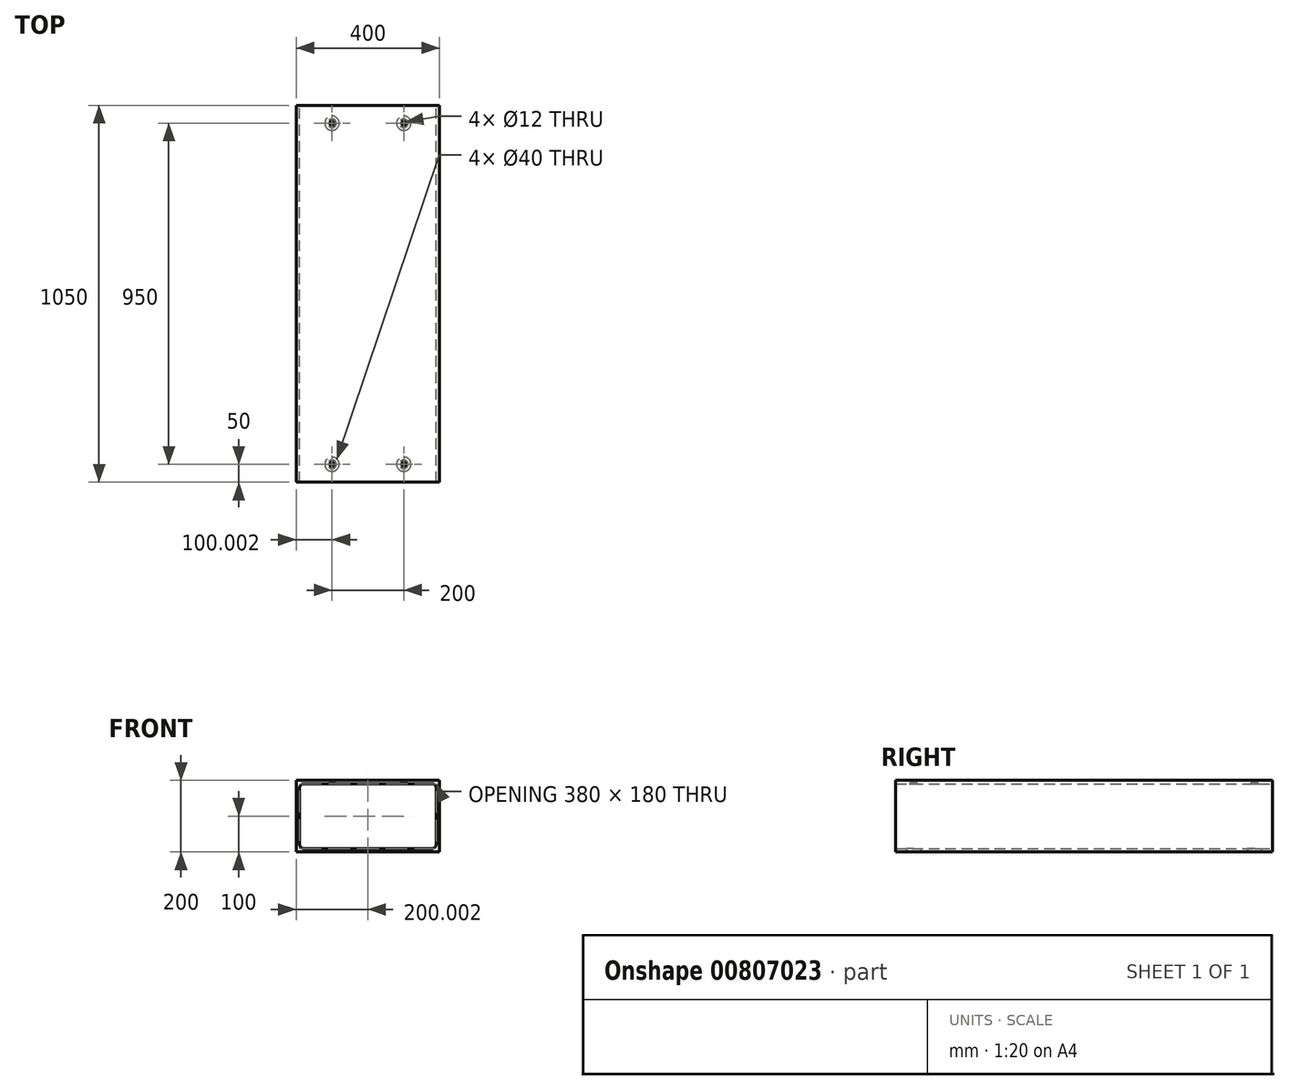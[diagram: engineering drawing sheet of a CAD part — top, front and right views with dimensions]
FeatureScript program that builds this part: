
annotation { "Feature Type Name" : "Feature", "Feature Type Description" : "" }
export const myFeature = defineFeature(function(context is Context, id is Id, definition is map)
    precondition{}
    {
        {
            var Q0;
            Q0=qCreatedBy(makeId("Front.planeOp"),FACE);
            var sketch = newSketch(context, id + "F0", { "sketchPlane" : qUnion([Q0])});
            skLineSegment(sketch, "E0.bottom", {"start": v(-139.55, 0) * mm, "end": v(260.45, 0) * mm});
            skLineSegment(sketch, "E0.top", {"start": v(-139.55, -200) * mm, "end": v(260.45, -200) * mm});
            skLineSegment(sketch, "E0.left", {"start": v(-139.55, 0) * mm, "end": v(-139.55, -200) * mm});
            skLineSegment(sketch, "E0.right", {"start": v(260.45, 0) * mm, "end": v(260.45, -200) * mm});
            skLineSegment(sketch, "E1.bottom", {"start": v(-119.55, -10) * mm, "end": v(240.45, -10) * mm});
            skLineSegment(sketch, "E1.top", {"start": v(-119.55, -190) * mm, "end": v(240.45, -190) * mm});
            skLineSegment(sketch, "E1.left", {"start": v(-129.55, -20) * mm, "end": v(-129.55, -180) * mm});
            skLineSegment(sketch, "E1.right", {"start": v(250.45, -20) * mm, "end": v(250.45, -180) * mm});
            skPoint(sketch, "E2.visualSharp", {"position": v(-129.55, -10) * mm});
            skArc(sketch, "E2.filletArc", {"start": v(-119.55, -10) * mm, "mid": v(-126.62, -12.93) * mm, "end": v(-129.55, -20) * mm});
            skPoint(sketch, "E3.visualSharp", {"position": v(250.45, -10) * mm});
            skArc(sketch, "E3.filletArc", {"start": v(250.45, -20) * mm, "mid": v(247.52, -12.93) * mm, "end": v(240.45, -10) * mm});
            skPoint(sketch, "E4.visualSharp", {"position": v(250.45, -190) * mm});
            skArc(sketch, "E4.filletArc", {"start": v(240.45, -190) * mm, "mid": v(247.52, -187.07) * mm, "end": v(250.45, -180) * mm});
            skPoint(sketch, "E5.visualSharp", {"position": v(-129.55, -190) * mm});
            skArc(sketch, "E5.filletArc", {"start": v(-129.55, -180) * mm, "mid": v(-126.62, -187.07) * mm, "end": v(-119.55, -190) * mm});
            skSolve(sketch);
        }
        {
            var Q0;
            Q0=makeQuery(id+"F0.imprint","IMPRINT",FACE,{"disambiguationData":[TD([[makeQuery(id+"F0.imprint","IMPRINT",EDGE,{"derivedFrom":sQuery(id+"F0.wireOp",EDGE,"E0.bottom")}),-1.0]])]});
            extrude(context, id + "F1", {"entities" : qUnion([Q0]), "endBound" : BoundingType.SYMMETRIC, "depth" : 1050 * mm, "offsetDistance" : 25 * mm});
        }
        {
            var Q0;
            Q0=makeQuery(id+"F1.opExtrude","SWEPT_FACE",FACE,{"disambiguationData":[OSD([sQuery(id+"F0.wireOp",EDGE,"E0.bottom")])]});
            var sketch = newSketch(context, id + "F2", { "sketchPlane" : qUnion([Q0])});
            skCircle(sketch, "E6", {"center": v(-39.55, -475) * mm, "radius": 6 * mm});
            skCircle(sketch, "E7", {"center": v(160.45, -475) * mm, "radius": 6 * mm});
            skCircle(sketch, "E8.MirrorC", {"center": v(-39.55, 475) * mm, "radius": 6 * mm});
            skCircle(sketch, "E9.MirrorC", {"center": v(160.45, 475) * mm, "radius": 6 * mm});
            skSolve(sketch);
        }
        {
            var Q0;
            Q0 = qSketchRegion(id + "F2", true);
            extrude(context, id + "F3", {"entities" : qUnion([Q0]), "operationType" : NewBodyOperationType.REMOVE, "endBound" : BoundingType.THROUGH_ALL, "oppositeDirection" : true, "depth" : 25 * mm, "offsetDistance" : 25 * mm});
        }
        {
            var Q0;
            Q0=makeQuery(id+"F1.opExtrude","SWEPT_FACE",FACE,{"disambiguationData":[OSD([sQuery(id+"F0.wireOp",EDGE,"E0.top")])]});
            var sketch = newSketch(context, id + "F4", { "sketchPlane" : qUnion([Q0])});
            skCircle(sketch, "E10", {"center": v(-39.55, 475) * mm, "radius": 20 * mm});
            skCircle(sketch, "E11", {"center": v(160.45, 475) * mm, "radius": 20 * mm});
            skCircle(sketch, "E12.MirrorC", {"center": v(-39.55, -475) * mm, "radius": 20 * mm});
            skCircle(sketch, "E13.MirrorC", {"center": v(160.45, -475) * mm, "radius": 20 * mm});
            skSolve(sketch);
        }
        {
            var Q0;
            Q0 = qSketchRegion(id + "F4", true);
            extrude(context, id + "F5", {"entities" : qUnion([Q0]), "operationType" : NewBodyOperationType.REMOVE, "oppositeDirection" : true, "depth" : 25 * mm, "offsetDistance" : 25 * mm});
        }
        {
            var Q0;
            Q0=makeQuery(id+"F3.boolean.opBoolean","INTERSECT",EDGE,{"derivedFrom":[makeQuery(id+"F1.opExtrude","SWEPT_FACE",FACE,{"disambiguationData":[OSD([sQuery(id+"F0.wireOp",EDGE,"E1.bottom")])]}),makeQuery(id+"F3.opExtrude","SWEPT_FACE",FACE,{"disambiguationData":[OSD([sQuery(id+"F2.wireOp",EDGE,"E6")])]})]});
            var Q1;
            Q1=makeQuery(id+"F3.boolean.opBoolean","INTERSECT",EDGE,{"derivedFrom":[makeQuery(id+"F1.opExtrude","SWEPT_FACE",FACE,{"disambiguationData":[OSD([sQuery(id+"F0.wireOp",EDGE,"E1.bottom")])]}),makeQuery(id+"F3.opExtrude","SWEPT_FACE",FACE,{"disambiguationData":[OSD([sQuery(id+"F2.wireOp",EDGE,"E7")])]})]});
            var Q2;
            Q2=makeQuery(id+"F3.boolean.opBoolean","INTERSECT",EDGE,{"derivedFrom":[makeQuery(id+"F1.opExtrude","SWEPT_FACE",FACE,{"disambiguationData":[OSD([sQuery(id+"F0.wireOp",EDGE,"E1.bottom")])]}),makeQuery(id+"F3.opExtrude","SWEPT_FACE",FACE,{"disambiguationData":[OSD([sQuery(id+"F2.wireOp",EDGE,"E8.MirrorC")])]})]});
            var Q3;
            Q3=makeQuery(id+"F3.boolean.opBoolean","INTERSECT",EDGE,{"derivedFrom":[makeQuery(id+"F1.opExtrude","SWEPT_FACE",FACE,{"disambiguationData":[OSD([sQuery(id+"F0.wireOp",EDGE,"E1.bottom")])]}),makeQuery(id+"F3.opExtrude","SWEPT_FACE",FACE,{"disambiguationData":[OSD([sQuery(id+"F2.wireOp",EDGE,"E9.MirrorC")])]})]});
            chamfer(context, id + "F6", {"entities" : qUnion([Q0, Q1, Q2, Q3]), "width" : 6 * mm, "tangentPropagation" : true});
        }
    });
